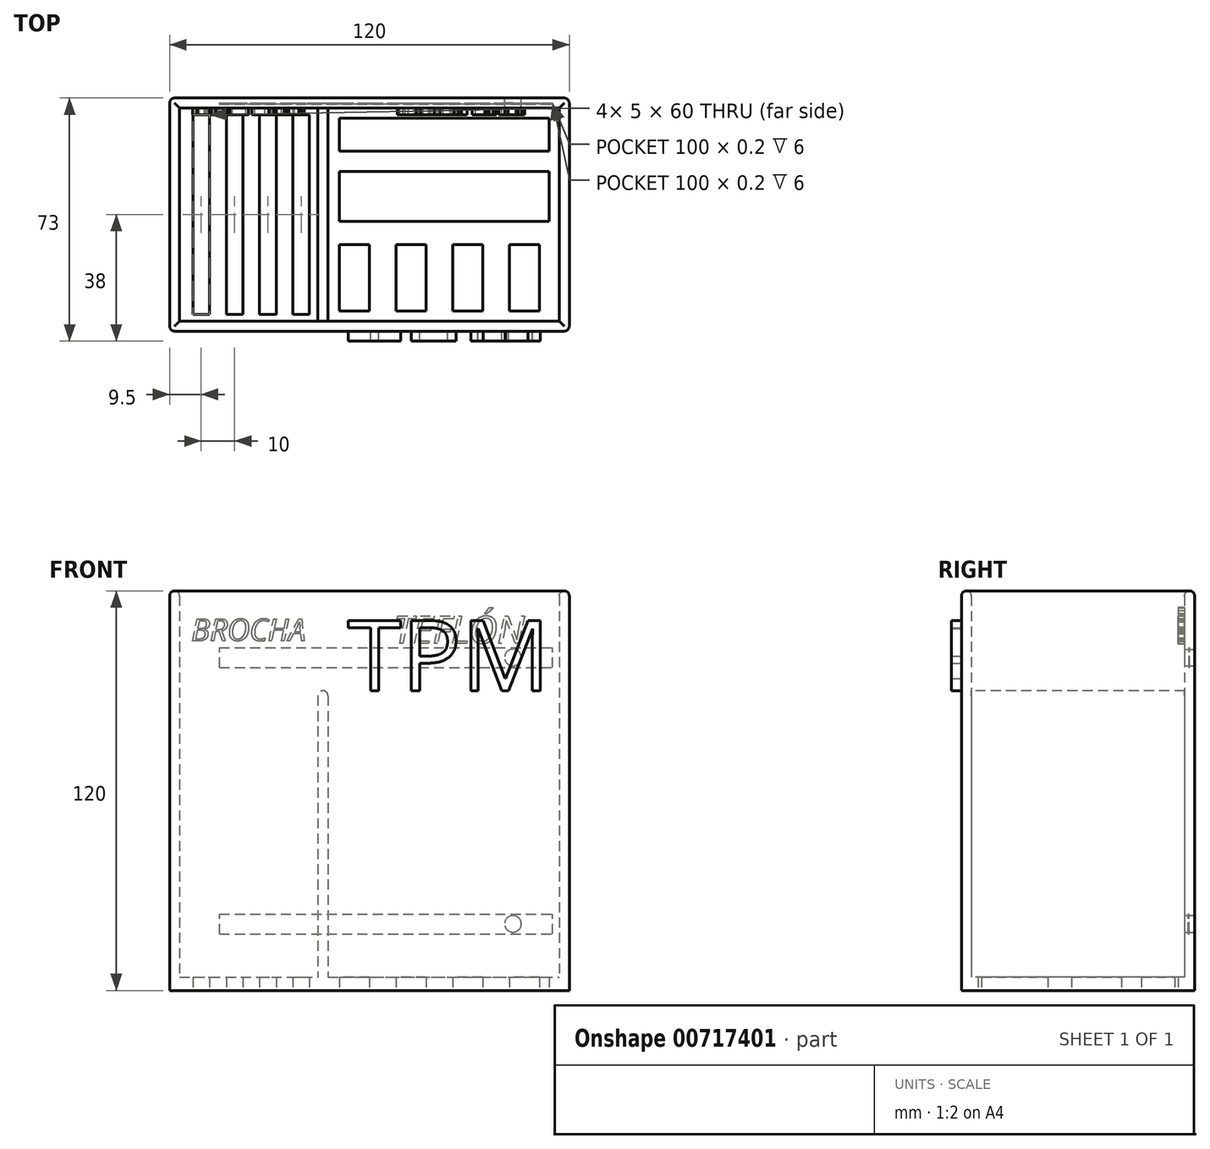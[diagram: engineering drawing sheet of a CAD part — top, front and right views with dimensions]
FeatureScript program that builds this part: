
annotation { "Feature Type Name" : "Feature", "Feature Type Description" : "" }
export const myFeature = defineFeature(function(context is Context, id is Id, definition is map)
    precondition{}
    {
        {
            var Q0;
            Q0=qCreatedBy(makeId("Top.planeOp"),FACE);
            var sketch = newSketch(context, id + "F0", { "sketchPlane" : qUnion([Q0])});
            skLineSegment(sketch, "E0.bottom", {"start": v(-60, 0) * mm, "end": v(60, 0) * mm});
            skLineSegment(sketch, "E0.top", {"start": v(-60, -70) * mm, "end": v(60, -70) * mm});
            skLineSegment(sketch, "E0.left", {"start": v(-60, 0) * mm, "end": v(-60, -70) * mm});
            skLineSegment(sketch, "E0.right", {"start": v(60, 0) * mm, "end": v(60, -70) * mm});
            skLineSegment(sketch, "E1.bottom", {"start": v(-57, -3) * mm, "end": v(57, -3) * mm});
            skLineSegment(sketch, "E1.top", {"start": v(-57, -67) * mm, "end": v(57, -67) * mm});
            skLineSegment(sketch, "E1.left", {"start": v(-57, -3) * mm, "end": v(-57, -67) * mm});
            skLineSegment(sketch, "E1.right", {"start": v(57, -3) * mm, "end": v(57, -67) * mm});
            skSolve(sketch);
        }
        {
            var Q0;
            Q0 = qSketchRegion(id + "F0", true);
            extrude(context, id + "F1", {"entities" : qUnion([Q0]), "depth" : 120 * mm, "offsetDistance" : 25 * mm});
        }
        {
            var Q0;
            Q0=qCreatedBy(makeId("Top.planeOp"),FACE);
            var sketch = newSketch(context, id + "F2", { "sketchPlane" : qUnion([Q0])});
            skLineSegment(sketch, "E2.bottom", {"start": v(-15.45, 0) * mm, "end": v(-12.45, 0) * mm});
            skLineSegment(sketch, "E2.top", {"start": v(-15.45, -67.85) * mm, "end": v(-12.45, -67.85) * mm});
            skLineSegment(sketch, "E2.left", {"start": v(-15.45, 0) * mm, "end": v(-15.45, -67.85) * mm});
            skLineSegment(sketch, "E2.right", {"start": v(-12.45, 0) * mm, "end": v(-12.45, -67.85) * mm});
            skSolve(sketch);
        }
        {
            var Q0;
            Q0 = qSketchRegion(id + "F2", true);
            extrude(context, id + "F3", {"entities" : qUnion([Q0]), "operationType" : NewBodyOperationType.ADD, "depth" : 90 * mm, "offsetDistance" : 25 * mm});
        }
        {
            var Q0;
            Q0=qCreatedBy(makeId("Top.planeOp"),FACE);
            var sketch = newSketch(context, id + "F4", { "sketchPlane" : qUnion([Q0])});
            skLineSegment(sketch, "E3.bottom", {"start": v(60, 0) * mm, "end": v(-60, 0) * mm});
            skLineSegment(sketch, "E3.top", {"start": v(60, -70) * mm, "end": v(-60, -70) * mm});
            skLineSegment(sketch, "E3.left", {"start": v(60, 0) * mm, "end": v(60, -70) * mm});
            skLineSegment(sketch, "E3.right", {"start": v(-60, 0) * mm, "end": v(-60, -70) * mm});
            skLineSegment(sketch, "E4.bottom", {"start": v(-53, -5) * mm, "end": v(-48, -5) * mm});
            skLineSegment(sketch, "E4.top", {"start": v(-53, -65) * mm, "end": v(-48, -65) * mm});
            skLineSegment(sketch, "E4.left", {"start": v(-53, -5) * mm, "end": v(-53, -65) * mm});
            skLineSegment(sketch, "E4.right", {"start": v(-48, -5) * mm, "end": v(-48, -65) * mm});
            skLineSegment(sketch, "E5.bottom", {"start": v(-43, -5) * mm, "end": v(-38, -5) * mm});
            skLineSegment(sketch, "E5.top", {"start": v(-43, -65) * mm, "end": v(-38, -65) * mm});
            skLineSegment(sketch, "E5.left", {"start": v(-43, -5) * mm, "end": v(-43, -65) * mm});
            skLineSegment(sketch, "E5.right", {"start": v(-38, -5) * mm, "end": v(-38, -65) * mm});
            skLineSegment(sketch, "E6.bottom", {"start": v(-33, -5) * mm, "end": v(-28, -5) * mm});
            skLineSegment(sketch, "E6.top", {"start": v(-33, -65) * mm, "end": v(-28, -65) * mm});
            skLineSegment(sketch, "E6.left", {"start": v(-33, -5) * mm, "end": v(-33, -65) * mm});
            skLineSegment(sketch, "E6.right", {"start": v(-28, -5) * mm, "end": v(-28, -65) * mm});
            skLineSegment(sketch, "E7.bottom", {"start": v(-9, -22) * mm, "end": v(54, -22) * mm});
            skLineSegment(sketch, "E8.bottom", {"start": v(-23, -5) * mm, "end": v(-18, -5) * mm});
            skLineSegment(sketch, "E8.top", {"start": v(-23, -65) * mm, "end": v(-18, -65) * mm});
            skLineSegment(sketch, "E8.left", {"start": v(-23, -5) * mm, "end": v(-23, -65) * mm});
            skLineSegment(sketch, "E8.right", {"start": v(-18, -5) * mm, "end": v(-18, -65) * mm});
            skLineSegment(sketch, "E9.bottom", {"start": v(-9, -37) * mm, "end": v(54, -37) * mm});
            skLineSegment(sketch, "E10", {"start": v(-9, -37) * mm, "end": v(-9, -22) * mm});
            skLineSegment(sketch, "E11", {"start": v(54, -37) * mm, "end": v(54, -22) * mm});
            skLineSegment(sketch, "E12", {"start": v(-9, -44) * mm, "end": v(-9, -64) * mm});
            skLineSegment(sketch, "E13", {"start": v(-9, -64) * mm, "end": v(0, -64) * mm});
            skLineSegment(sketch, "E14", {"start": v(0, -64) * mm, "end": v(0, -44) * mm});
            skLineSegment(sketch, "E15", {"start": v(0, -44) * mm, "end": v(-9, -44) * mm});
            skLineSegment(sketch, "E16", {"start": v(8, -44) * mm, "end": v(8, -64) * mm});
            skLineSegment(sketch, "E17", {"start": v(8, -64) * mm, "end": v(17, -64) * mm});
            skLineSegment(sketch, "E18", {"start": v(17, -64) * mm, "end": v(17, -44) * mm});
            skLineSegment(sketch, "E19", {"start": v(17, -44) * mm, "end": v(8, -44) * mm});
            skLineSegment(sketch, "E20", {"start": v(25, -44) * mm, "end": v(25, -64) * mm});
            skLineSegment(sketch, "E21", {"start": v(25, -64) * mm, "end": v(34, -64) * mm});
            skLineSegment(sketch, "E22", {"start": v(34, -64) * mm, "end": v(34, -44) * mm});
            skLineSegment(sketch, "E23", {"start": v(34, -44) * mm, "end": v(25, -44) * mm});
            skLineSegment(sketch, "E24", {"start": v(42, -44) * mm, "end": v(42, -64) * mm});
            skLineSegment(sketch, "E25", {"start": v(42, -64) * mm, "end": v(51, -64) * mm});
            skLineSegment(sketch, "E26", {"start": v(51, -64) * mm, "end": v(51, -44) * mm});
            skLineSegment(sketch, "E27", {"start": v(51, -44) * mm, "end": v(42, -44) * mm});
            skLineSegment(sketch, "E28.bottom", {"start": v(-9, -6) * mm, "end": v(54, -6) * mm});
            skLineSegment(sketch, "E29.bottom", {"start": v(-9, -16) * mm, "end": v(54, -16) * mm});
            skLineSegment(sketch, "E30", {"start": v(-9, -16) * mm, "end": v(-9, -6) * mm});
            skLineSegment(sketch, "E31", {"start": v(54, -16) * mm, "end": v(54, -6) * mm});
            skSolve(sketch);
        }
        {
            var Q0;
            Q0 = qSketchRegion(id + "F2", true);
            var Q1;
            Q1 = qSketchRegion(id + "F4", true);
            extrude(context, id + "F5", {"entities" : qUnion([Q0, Q1]), "operationType" : NewBodyOperationType.ADD, "depth" : 4 * mm, "offsetDistance" : 25 * mm});
        }
        {
            var Q0;
            Q0=makeQuery(id+"F1.opExtrude","CAP_EDGE",EDGE,{"disambiguationData":[OSD([sQuery(id+"F0.wireOp",EDGE,"E0.left")])],"isStart":false});
            var Q1;
            Q1=makeQuery(id+"F1.opExtrude","CAP_EDGE",EDGE,{"disambiguationData":[OSD([sQuery(id+"F0.wireOp",EDGE,"E0.top")])],"isStart":false});
            var Q2;
            Q2=makeQuery(id+"F1.opExtrude","CAP_EDGE",EDGE,{"disambiguationData":[OSD([sQuery(id+"F0.wireOp",EDGE,"E0.right")])],"isStart":false});
            var Q3;
            Q3=makeQuery(id+"F1.opExtrude","CAP_EDGE",EDGE,{"disambiguationData":[OSD([sQuery(id+"F0.wireOp",EDGE,"E0.bottom")])],"isStart":false});
            var Q4;
            Q4=makeQuery(id+"F1.opExtrude","SWEPT_EDGE",EDGE,{"disambiguationData":[OSD([sQuery(id+"F0.wireOp",EDGE,"E0.bottom"),sQuery(id+"F0.wireOp",EDGE,"E0.right")])]});
            var Q5;
            Q5=makeQuery(id+"F1.opExtrude","SWEPT_EDGE",EDGE,{"disambiguationData":[OSD([sQuery(id+"F0.wireOp",EDGE,"E0.top"),sQuery(id+"F0.wireOp",EDGE,"E0.right")])]});
            var Q6;
            Q6=makeQuery(id+"F1.opExtrude","SWEPT_EDGE",EDGE,{"disambiguationData":[OSD([sQuery(id+"F0.wireOp",EDGE,"E0.top"),sQuery(id+"F0.wireOp",EDGE,"E0.left")])]});
            var Q7;
            Q7=makeQuery(id+"F1.opExtrude","SWEPT_EDGE",EDGE,{"disambiguationData":[OSD([sQuery(id+"F0.wireOp",EDGE,"E0.bottom"),sQuery(id+"F0.wireOp",EDGE,"E0.left")])]});
            fillet(context, id + "F6", {"entities" : qUnion([Q0, Q1, Q2, Q3, Q4, Q5, Q6, Q7]), "radius" : 1.5 * mm, "tangentPropagation" : true, "allowEdgeOverflow" : false});
        }
        {
            var Q0;
            Q0=qCreatedBy(makeId("Front.planeOp"),FACE);
            var sketch = newSketch(context, id + "F7", { "sketchPlane" : qUnion([Q0])});
            skLineSegment(sketch, "E32.bottom", {"start": v(50.6, 115) * mm, "end": v(35.6, 115) * mm});
            skLineSegment(sketch, "E32.top", {"start": v(50.6, 0) * mm, "end": v(35.6, 0) * mm});
            skLineSegment(sketch, "E32.left", {"start": v(50.6, 115) * mm, "end": v(50.6, 0) * mm});
            skLineSegment(sketch, "E32.right", {"start": v(35.6, 115) * mm, "end": v(35.6, 0) * mm});
            skLineSegment(sketch, "E33.bottom", {"start": v(35.6, 0) * mm, "end": v(-56.48, 0) * mm});
            skLineSegment(sketch, "E33.top", {"start": v(35.6, 6.66) * mm, "end": v(-56.48, 6.66) * mm});
            skLineSegment(sketch, "E33.left", {"start": v(35.6, 0) * mm, "end": v(35.6, 6.66) * mm});
            skLineSegment(sketch, "E33.right", {"start": v(-56.48, 0) * mm, "end": v(-56.48, 6.66) * mm});
            skSolve(sketch);
        }
        {
            var Q0;
            Q0=qCreatedBy(makeId("Front.planeOp"),FACE);
            var sketch = newSketch(context, id + "F8", { "sketchPlane" : qUnion([Q0])});
            skCircle(sketch, "E34", {"center": v(43.1, 100) * mm, "radius": 2.5 * mm});
            skCircle(sketch, "E35", {"center": v(43.1, 20) * mm, "radius": 2.5 * mm});
            skSolve(sketch);
        }
        {
            var Q0;
            Q0 = qSketchRegion(id + "F8", true);
            extrude(context, id + "F9", {"entities" : qUnion([Q0]), "operationType" : NewBodyOperationType.REMOVE, "depth" : 25 * mm, "offsetDistance" : 25 * mm, "hasSecondDirection" : true, "secondDirectionOppositeDirection" : true, "secondDirectionDepth" : 25 * mm});
        }
        {
            var Q0;
            Q0=makeQuery(id+"F1.opExtrude","SWEPT_FACE",FACE,{"disambiguationData":[OSD([sQuery(id+"F0.wireOp",EDGE,"E0.top")])]});
            var sketch = newSketch(context, id + "F10", { "sketchPlane" : qUnion([Q0])});
            skText(sketch, "E36", { "text": "TPM", "fontName": "OpenSans-Regular.ttf"});
            const initialGuessF10  = {"E36": [-0.00663, 0.09, 1, 0, 0.02128]};
            skSetInitialGuess(sketch, initialGuessF10);
            skSolve(sketch);
        }
        {
            var Q0;
            Q0 = qSketchRegion(id + "F10", true);
            extrude(context, id + "F11", {"entities" : qUnion([Q0]), "operationType" : NewBodyOperationType.ADD, "depth" : 3 * mm, "offsetDistance" : 25 * mm});
        }
        {
            var Q0;
            Q0=makeQuery(id+"F1.opExtrude","CAP_EDGE",EDGE,{"disambiguationData":[OSD([sQuery(id+"F0.wireOp",EDGE,"E1.left")])],"isStart":false});
            var Q1;
            Q1=makeQuery(id+"F1.opExtrude","CAP_EDGE",EDGE,{"disambiguationData":[OSD([sQuery(id+"F0.wireOp",EDGE,"E1.bottom")])],"isStart":false});
            var Q2;
            Q2=makeQuery(id+"F1.opExtrude","CAP_EDGE",EDGE,{"disambiguationData":[OSD([sQuery(id+"F0.wireOp",EDGE,"E1.top")])],"isStart":false});
            var Q3;
            Q3=makeQuery(id+"F1.opExtrude","CAP_EDGE",EDGE,{"disambiguationData":[OSD([sQuery(id+"F0.wireOp",EDGE,"E1.right")])],"isStart":false});
            fillet(context, id + "F12", {"entities" : qUnion([Q0, Q1, Q2, Q3]), "radius" : 1.5 * mm, "tangentPropagation" : true, "allowEdgeOverflow" : false});
        }
        {
            var Q0;
            Q0=makeQuery(id+"F3.opExtrude","CAP_EDGE",EDGE,{"disambiguationData":[OSD([sQuery(id+"F2.wireOp",EDGE,"E2.right")])],"isStart":false});
            var Q1;
            Q1=makeQuery(id+"F3.opExtrude","CAP_EDGE",EDGE,{"disambiguationData":[OSD([sQuery(id+"F2.wireOp",EDGE,"E2.left")])],"isStart":false});
            fillet(context, id + "F13", {"entities" : qUnion([Q0, Q1]), "radius" : 1.5 * mm, "tangentPropagation" : true, "allowEdgeOverflow" : false});
        }
        {
            var Q0;
            Q0=qCreatedBy(makeId("Top.planeOp"),FACE);
            cPlane(context, id + "F14", {"entities" : qUnion([Q0]), "cplaneType" : CPlaneType.OFFSET, "offset" : 20 * mm, "width" : 150 * mm, "height" : 150 * mm});
        }
        {
            var Q0;
            Q0=qCreatedBy(id+"F14.planeOp",FACE);
            cPlane(context, id + "F15", {"entities" : qUnion([Q0]), "cplaneType" : CPlaneType.OFFSET, "offset" : 80 * mm, "width" : 150 * mm, "height" : 150 * mm});
        }
        {
            var Q0;
            Q0=qCreatedBy(id+"F14.planeOp",FACE);
            var sketch = newSketch(context, id + "F16", { "sketchPlane" : qUnion([Q0])});
            skLineSegment(sketch, "E37.bottom", {"start": v(-45, -1.88) * mm, "end": v(55, -1.88) * mm});
            skLineSegment(sketch, "E37.top", {"start": v(-45, -1.68) * mm, "end": v(55, -1.68) * mm});
            skLineSegment(sketch, "E37.left", {"start": v(-45, -1.88) * mm, "end": v(-45, -1.68) * mm});
            skLineSegment(sketch, "E37.right", {"start": v(55, -1.88) * mm, "end": v(55, -1.68) * mm});
            skSolve(sketch);
        }
        {
            var Q0;
            Q0 = qSketchRegion(id + "F16", true);
            extrude(context, id + "F17", {"entities" : qUnion([Q0]), "operationType" : NewBodyOperationType.REMOVE, "oppositeDirection" : true, "depth" : 3 * mm, "offsetDistance" : 25 * mm, "hasSecondDirection" : true, "secondDirectionOppositeDirection" : false, "secondDirectionDepth" : 3 * mm});
        }
        {
            var Q0;
            Q0=qCreatedBy(id+"F15.planeOp",FACE);
            var sketch = newSketch(context, id + "F18", { "sketchPlane" : qUnion([Q0])});
            skLineSegment(sketch, "E38.bottom", {"start": v(-45, -1.7) * mm, "end": v(55, -1.7) * mm});
            skLineSegment(sketch, "E38.top", {"start": v(-45, -1.5) * mm, "end": v(55, -1.5) * mm});
            skLineSegment(sketch, "E38.left", {"start": v(-45, -1.7) * mm, "end": v(-45, -1.5) * mm});
            skLineSegment(sketch, "E38.right", {"start": v(55, -1.7) * mm, "end": v(55, -1.5) * mm});
            skSolve(sketch);
        }
        {
            var Q0;
            Q0 = qSketchRegion(id + "F18", true);
            extrude(context, id + "F19", {"entities" : qUnion([Q0]), "operationType" : NewBodyOperationType.REMOVE, "oppositeDirection" : true, "depth" : 3 * mm, "offsetDistance" : 25 * mm, "hasSecondDirection" : true, "secondDirectionOppositeDirection" : false, "secondDirectionDepth" : 3 * mm});
        }
        {
            var Q0;
            Q0=makeQuery(id+"F1.opExtrude","SWEPT_FACE",FACE,{"disambiguationData":[OSD([sQuery(id+"F0.wireOp",EDGE,"E1.bottom")])]});
            var sketch = newSketch(context, id + "F20", { "sketchPlane" : qUnion([Q0])});
            skText(sketch, "E39", { "text": "BROCHA", "fontName": "OpenSans-Italic.ttf"});
            skText(sketch, "E40", { "text": "TEFLÓN", "fontName": "OpenSans-Italic.ttf"});
            const initialGuessF20  = {"E39": [-0.05349, 0.105, 1, 0, 0.00668], "E40": [0.0073, 0.10417, 1, 0, 0.00836]};
            skSetInitialGuess(sketch, initialGuessF20);
            skSolve(sketch);
        }
        {
            var Q0;
            Q0 = qSketchRegion(id + "F20", true);
            extrude(context, id + "F21", {"entities" : qUnion([Q0]), "operationType" : NewBodyOperationType.ADD, "depth" : 2 * mm, "offsetDistance" : 25 * mm});
        }
    });
